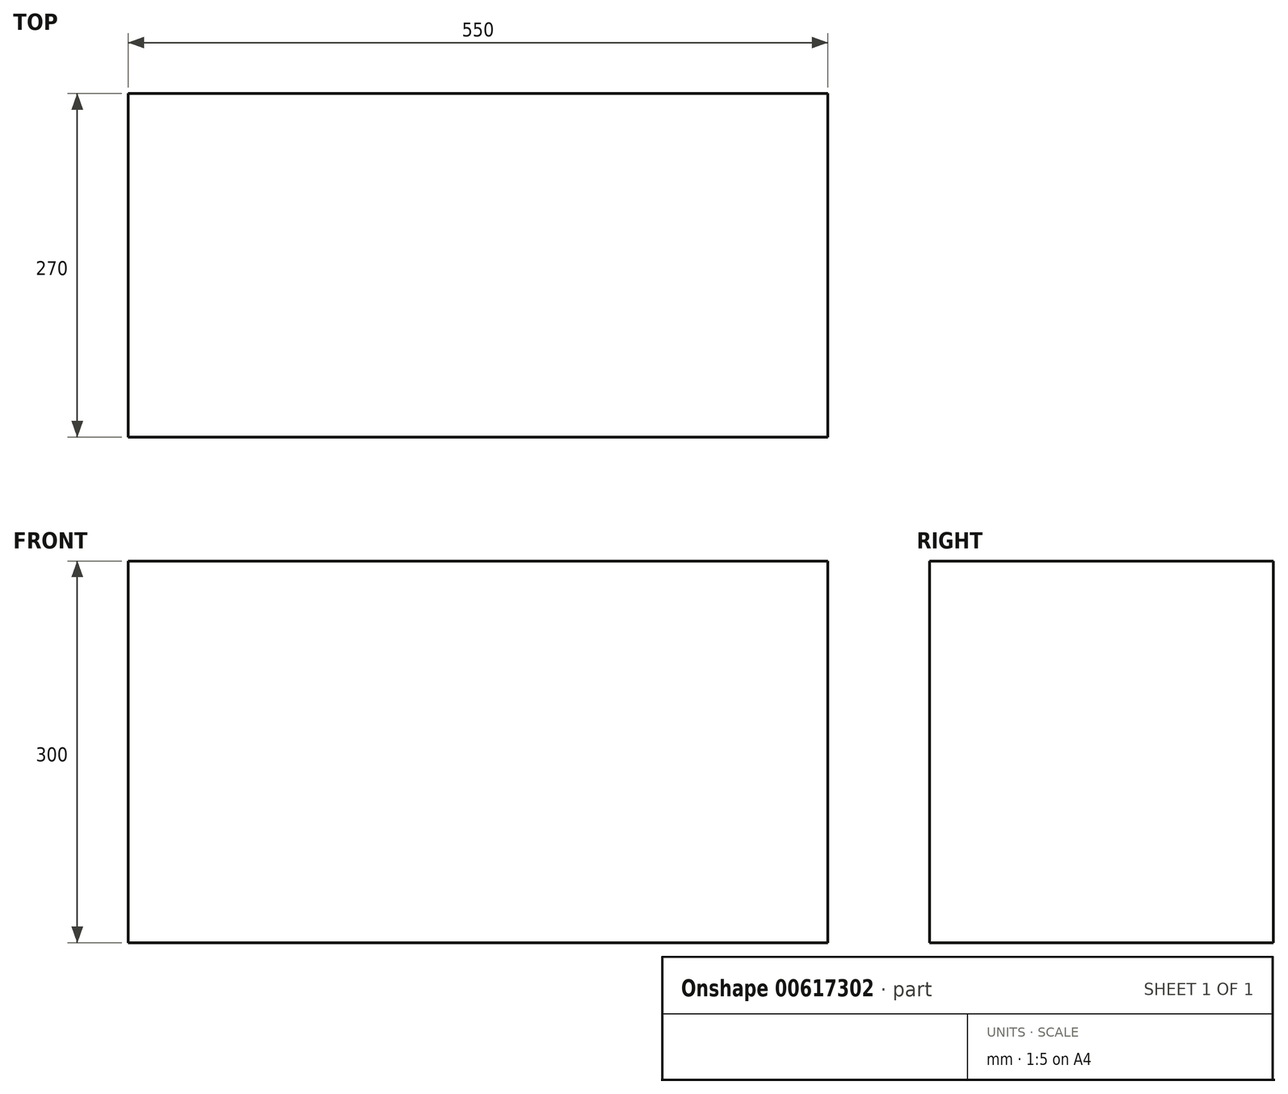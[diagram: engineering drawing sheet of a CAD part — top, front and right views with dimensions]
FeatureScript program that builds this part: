
annotation { "Feature Type Name" : "Feature", "Feature Type Description" : "" }
export const myFeature = defineFeature(function(context is Context, id is Id, definition is map)
    precondition{}
    {
        {
            var Q0;
            Q0=qCreatedBy(makeId("Top.planeOp"),FACE);
            var sketch = newSketch(context, id + "F0", { "sketchPlane" : qUnion([Q0])});
            skLineSegment(sketch, "E0.bottom", {"start": v(-237.98, 17.51) * mm, "end": v(312.02, 17.51) * mm});
            skLineSegment(sketch, "E0.top", {"start": v(-237.98, -252.49) * mm, "end": v(312.02, -252.49) * mm});
            skLineSegment(sketch, "E0.left", {"start": v(-237.98, 17.51) * mm, "end": v(-237.98, -252.49) * mm});
            skLineSegment(sketch, "E0.right", {"start": v(312.02, 17.51) * mm, "end": v(312.02, -252.49) * mm});
            skSolve(sketch);
        }
        {
            var Q0;
            Q0 = qSketchRegion(id + "F0", true);
            extrude(context, id + "F1", {"entities" : qUnion([Q0]), "depth" : 300 * mm, "offsetDistance" : 25 * mm});
        }
    });
